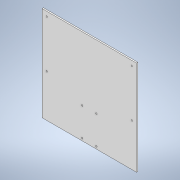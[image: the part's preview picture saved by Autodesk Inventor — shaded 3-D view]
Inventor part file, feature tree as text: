
AUTODESK INVENTOR PART (.ipt)
format: ipt  version: 2021 (Build 250183000, 183)  size: 121,856 bytes
history: native  units: mm
features: extrude x1, sketch x1
ambient origin geometry x8: Origin, YZ Plane, XZ Plane, XY Plane, X Axis, Y Axis, Z Axis, Center Point
bodies: Solid1 (feature_tree)
feature tree (2):
  extrude  "Extrusion1"  Depth=200.0mm
  sketch  "Sketch1"  dims[d0=200.0mm d1=200.0mm d2=3.0mm d3=3.0mm d4=5.0mm d5=5.0mm d6=30.0mm d7=85.0mm d8=3.0mm d9=3.0mm d10=85.0mm d11=60.0mm d12=30.0mm d13=60.0mm d14=3.0mm d15=3.0mm d16=10.0mm d17=10.0mm d18=10.0mm d19=10.0mm d20=3.0mm d21=3.0mm d22=10.0mm d23=10.0mm d24=100.0mm d25=100.0mm d26=3.0mm d27=0.0mm]
